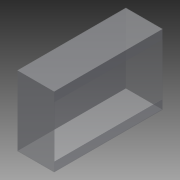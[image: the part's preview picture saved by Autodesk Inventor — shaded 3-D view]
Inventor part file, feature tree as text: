
AUTODESK INVENTOR PART (.ipt)
format: ipt  version: 2013 (Build 170138000, 138)  size: 91,136 bytes
history: native  units: in
note: dims shown in document units (in); Inventor stores cm internally (conversion verified against a paired STEP export)
features: extrude x2, sketch x2, shell x1
ambient origin geometry x8: Origin, YZ Plane, XZ Plane, XY Plane, X Axis, Y Axis, Z Axis, Center Point
bodies: Solid1 (feature_tree)
feature tree (5):
  extrude  "Extrusion1"  Depth=20.0in
  shell  "Shell1"  Thickness=38.0in
  extrude  "Extrusion2"  Depth=5.0in
  sketch  "Sketch1"  dims[d0=59.0in d1=20.0in d2=38.0in d3=0.0in]
  sketch  "Sketch2"  dims[d4=0.125in d5=5.0in d6=5.0in d7=0.125in d8=0.0in]
